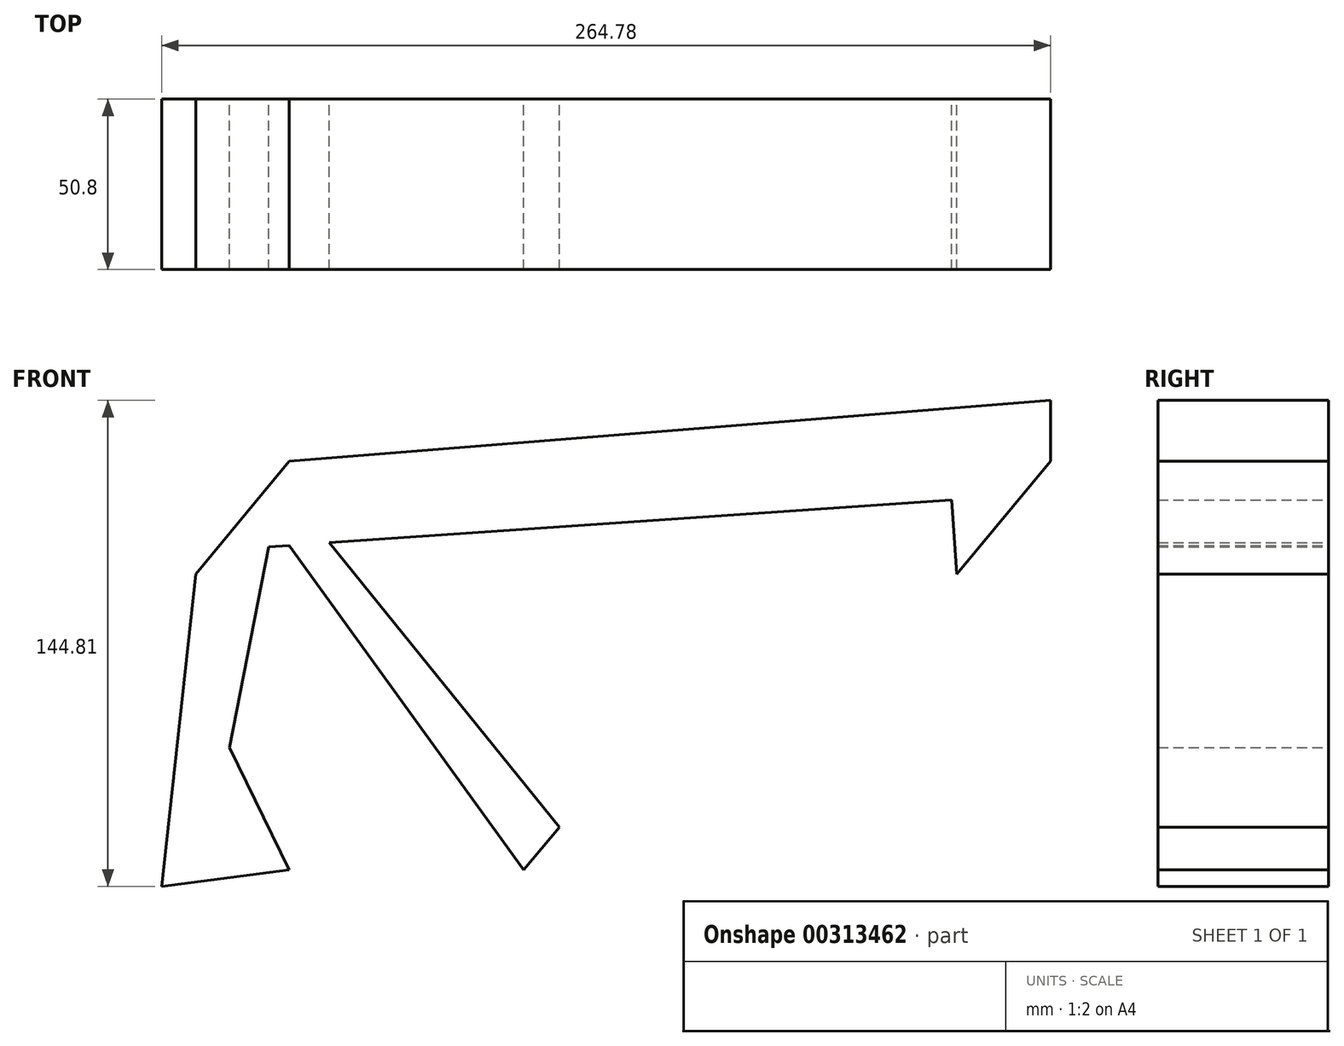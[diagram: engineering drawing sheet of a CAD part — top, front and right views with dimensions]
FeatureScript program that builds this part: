
annotation { "Feature Type Name" : "Feature", "Feature Type Description" : "" }
export const myFeature = defineFeature(function(context is Context, id is Id, definition is map)
    precondition{}
    {
        {
            var Q0;
            Q0=qCreatedBy(makeId("Front.planeOp"),FACE);
            var sketch = newSketch(context, id + "F0", { "sketchPlane" : qUnion([Q0])});
            skLineSegment(sketch, "E0", {"start": v(-136.68, -58.76) * mm, "end": v(-154.45, -22.22) * mm});
            skLineSegment(sketch, "E1", {"start": v(-154.45, -22.22) * mm, "end": v(-142.8, 37.53) * mm});
            skLineSegment(sketch, "E2", {"start": v(-142.8, 37.53) * mm, "end": v(60.68, 51.53) * mm});
            skLineSegment(sketch, "E3", {"start": v(60.68, 51.53) * mm, "end": v(62.2, 29.43) * mm});
            skLineSegment(sketch, "E4", {"start": v(62.2, 29.43) * mm, "end": v(90.1, 63.09) * mm});
            skLineSegment(sketch, "E5", {"start": v(90.1, 63.09) * mm, "end": v(90.1, 81.2) * mm});
            skLineSegment(sketch, "E6", {"start": v(90.1, 81.2) * mm, "end": v(-136.68, 63.09) * mm});
            skLineSegment(sketch, "E7", {"start": v(-136.68, 63.09) * mm, "end": v(-164.58, 29.43) * mm});
            skLineSegment(sketch, "E8", {"start": v(-164.58, 29.43) * mm, "end": v(-174.68, -63.6) * mm});
            skLineSegment(sketch, "E9", {"start": v(-174.68, -63.6) * mm, "end": v(-136.68, -58.76) * mm});
            skLineSegment(sketch, "E10", {"start": v(90.1, 81.2) * mm, "end": v(60.68, 51.53) * mm});
            skLineSegment(sketch, "E11", {"start": v(-136.68, 37.95) * mm, "end": v(-66.8, -58.76) * mm});
            skLineSegment(sketch, "E12", {"start": v(-66.8, -58.76) * mm, "end": v(-56.22, -46) * mm});
            skLineSegment(sketch, "E13", {"start": v(-56.22, -46) * mm, "end": v(-124.72, 38.77) * mm});
            skLineSegment(sketch, "E14", {"start": v(-124.72, 38.77) * mm, "end": v(-136.68, 37.95) * mm});
            skSolve(sketch);
        }
        {
            var Q0;
            Q0=makeQuery(id+"F0.imprint","IMPRINT",FACE,{"disambiguationData":[TD([[makeQuery(id+"F0.imprint","IMPRINT",EDGE,{"derivedFrom":sQuery(id+"F0.wireOp",EDGE,"E0")}),1.0]])]});
            var Q1;
            Q1=makeQuery(id+"F0.imprint","IMPRINT",FACE,{"disambiguationData":[TD([[makeQuery(id+"F0.imprint","IMPRINT",EDGE,{"derivedFrom":sQuery(id+"F0.wireOp",EDGE,"E11")}),1.0]])]});
            var Q2;
            Q2=makeQuery(id+"F0.imprint","IMPRINT",FACE,{"disambiguationData":[TD([[makeQuery(id+"F0.imprint","IMPRINT",EDGE,{"derivedFrom":sQuery(id+"F0.wireOp",EDGE,"E3")}),1.0]])]});
            extrude(context, id + "F1", {"entities" : qUnion([Q0, Q1, Q2]), "depth" : 25.4 * mm});
        }
        {
            var Q0;
            Q0=makeQuery(id+"F1.opExtrude","CAP_FACE",FACE,{"disambiguationData":[OSD([sQuery(id+"F0.wireOp",EDGE,"E0"),sQuery(id+"F0.wireOp",EDGE,"E1"),sQuery(id+"F0.wireOp",EDGE,"E2"),sQuery(id+"F0.wireOp",EDGE,"E3"),sQuery(id+"F0.wireOp",EDGE,"E4"),sQuery(id+"F0.wireOp",EDGE,"E5"),sQuery(id+"F0.wireOp",EDGE,"E6"),sQuery(id+"F0.wireOp",EDGE,"E7"),sQuery(id+"F0.wireOp",EDGE,"E8"),sQuery(id+"F0.wireOp",EDGE,"E9"),sQuery(id+"F0.wireOp",EDGE,"E11"),sQuery(id+"F0.wireOp",EDGE,"E12"),sQuery(id+"F0.wireOp",EDGE,"E13")])],"isStart":false});
            extrude(context, id + "F2", {"entities" : qUnion([Q0]), "operationType" : NewBodyOperationType.ADD, "depth" : 25.4 * mm});
        }
    });
